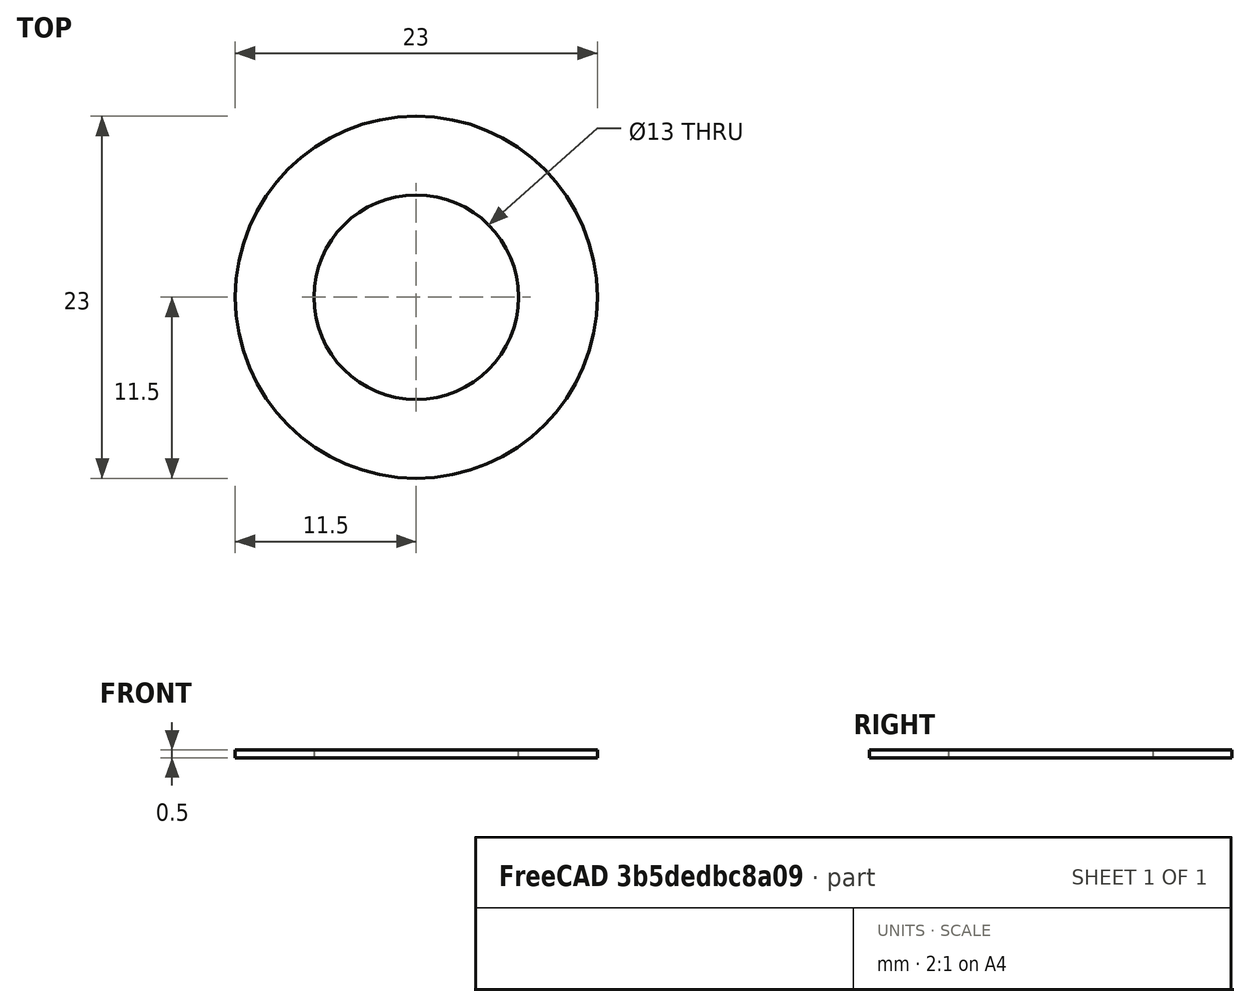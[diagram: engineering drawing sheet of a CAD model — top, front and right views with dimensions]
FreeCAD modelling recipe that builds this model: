
FCSTD DOCUMENT  (FreeCAD 0.19R24276 (Git))
Label: Ring_d13_d23_h0_5_v3
License: All rights reserved
LicenseURL: http://en.wikipedia.org/wiki/All_rights_reserved
objects: Sketcher::SketchObject×1, PartDesign::Pad×1, PartDesign::Body×1
note: 4 computed .brp shape members not serialized (recipe doc carries the construction recipe); baked Part::Feature solids carry a one-line shape summary decoded from their .brp

FEATURE [Sketcher::SketchObject] Sketch
  FullyConstrained = true
  MapMode = 5
  Support = -> [XY_Plane]
  sketch-geometry (2):
    g0: Circle CenterX=0 CenterY=0 CenterZ=0 NormalX=0 NormalY=0 NormalZ=1 AngleXU=0 Radius=6.5
    g1: Circle CenterX=0 CenterY=0 CenterZ=0 NormalX=0 NormalY=0 NormalZ=1 AngleXU=0 Radius=11.5
  constraints (4):
    c: Coincident(g0,g-1)
    c: Coincident(g1,g0)
    c: Diameter(g0) = 13
    c: Diameter(g1) = 23
FEATURE [PartDesign::Pad] Pad
  Direction = (1,1,1)
  Length = 0.5
  Length2 = 100
  Profile = -> Sketch
  Type = 0
FEATURE [PartDesign::Body] Body
  Group = -> [Sketch,Pad]
  Origin = -> Origin
  Tip = -> Pad
